# Revit family: Charon HSD-E01
name_source: partatom
category: Türen
revit_build: Autodesk Revit 2016 (Build: 20150220_1215(x64)
units: mm (PartAtom-declared; Revit-internal decimal feet)

## family parameters
Arbeitsebenenbasiert = Nein
Beim Laden mit Abzugskörper schneiden = Nein
Gemeinsam genutzt = Nein
Immer vertikal = Ja
Raumberechnungspunkt = Nein

## types (3) — shared parameters
Analytische Konstruktion = <Keine Auswahl>
Date of publishing = 1/16/2017
Design country = Germany
Edition number = 1
Manufacturer = Kaba GmbH
Manufacturer country = Germany
Manufacturer name = DORMA
Material main = Metal
Nominal height = 900
Nominal width = 970
Product SKU = Charon_HSD-E01
StandardUsed = 1
Technical description = http://www.kaba.com
Type = Charon HSD-E01
URL = http://www.kaba.com

## per-type parameters (varying)
| type | AccessWidth | BarrierHeight | HasGlass |
| Charon HSD-E01 900 | 900 mm  [stored 2.95276 ft] | 900 mm  [stored 2.95276 ft] | Nein |
| Charon HSD-E01 1000 | 900 mm  [stored 2.95276 ft] | 1000 mm  [stored 3.28084 ft] | Ja |
| Charon HSD-E01 1100 | 1000 mm  [stored 3.28084 ft] | 1100 mm | Ja |

note: [stored X ft] marks values corroborated as IEEE doubles in the binary element streams (Revit-internal decimal feet)
